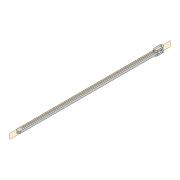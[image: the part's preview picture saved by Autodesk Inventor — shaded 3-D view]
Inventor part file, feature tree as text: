
AUTODESK INVENTOR PART (.ipt)
format: ipt  version: 2022 (Build 260153000, 153)  size: 159,744 bytes
history: native  units: mm
features: extrude x6, sketch x5, projected_geometry x4
ambient origin geometry x8: Origin, YZ Plane, XZ Plane, XY Plane, X Axis, Y Axis, Z Axis, Center Point
bodies: Solid1 (feature_tree)
feature tree (15):
  extrude  "Extrusion1"  Depth=10.0mm
  sketch  "Sketch2"  dims[d3=399.562mm d6=6.0mm d7=0.0mm]
  extrude  "Extrusion2"  Depth=6.0mm TaperAngle=0.0deg
  extrude  "Extrusion3"  Depth=3.3mm
  extrude  "Extrusion4"  Depth=10.0mm
  extrude  "Extrusion5"  Depth=4.0mm TaperAngle=0.0deg
  extrude  "Extrusion6"  Depth=10.0mm
  sketch  "Sketch1"  dims[d1=3.3mm d2=10.0mm]
  projected_geometry  "Projected Loop1"
  sketch  "Sketch3"  dims[d16=3.3mm d17=20.0mm]
  projected_geometry  "Projected Loop2"
  sketch  "Sketch4"  dims[d18=10.0mm d20=15.0mm]
  projected_geometry  "Projected Loop3"
  sketch  "Sketch5"  dims[d21=10.0mm d22=4.0mm d23=0.0mm d24=10.0mm d25=15.0mm d26=4.0mm d27=0.0mm d28=6.0mm d29=0.0mm d30=0.2mm d31=0.0mm d32=0.2mm d33=0.0mm]
  projected_geometry  "Projected Loop4"
